# Revit family: ATPSF-101-120-S REV2
name_source: partatom
category: Mechanical Equipment
revit_build: Autodesk Revit 2017 (Build: 20190508_0315(x64)
units: mm (PartAtom-declared; Revit-internal decimal feet)

## family parameters
Always vertical = Yes
Cut with Voids When Loaded = No
OmniClass Number = 23.75.00.00
OmniClass Title = Climate Control (HVAC)
Part Type = Normal
Room Calculation Point = No
Round Connector Dimension = Use Diameter
Shared = No
Work Plane-Based = No

## types (10) — shared parameters
1-1/2HP = No
2HP = No
Base Height = 5' - 9 7/8"
Base Lenglth = 2' - 6 1/2"
Base Width = 1' - 10 1/2"
Description = Automatic Fuel Oil Transfer Pump Set
Inlet Diameter = 0' - 1"
Inlet Radius = 0' - 0 1/2"
Manufacturer = Preferred Utilities MFG
Outlet Diameter = 0' - 0 1/2"
Outlet Radius = 0' - 0 1/4"
Relief Valve Diameter = 0' - 0 1/2"
Relief Valve Radius = 0' - 0 1/4"
URL = www.preferred-mfg.com
Weight = 450.00 lbf

## per-type parameters (varying)
| type | 1/2HP | 1/3HP | 115/208/230 Volts | 1HP | 208/230/460 Volts | 3/4HP | G.P.H. Oil #2 / #4 | HP | Model | PSI | Phase | RPM |
| 101-S_23/24 GPH_100 PSI_1/3 HP_1725 RPM | No | Yes | Yes | No | No | No | 23 / 24 | 1/3 | ATPSF-101-S | 100.00 psi | 1 | 1725 |
| 101-S_24/25 GPH_50 PSI_1/3 HP_1725 RPM | No | Yes | Yes | No | No | No | 24 / 25 | 1/3 | ATPSF-101-S | 50.00 psi | 1 | 1725 |
| 102-S_51/54 GPH_100 PSI_1/3 HP_1725 RPM | No | Yes | Yes | No | No | No | 51 / 54 | 1/3 | ATPSF-102-S | 100.00 psi | 1 | 1725 |
| 102-S_54/56 GPH_50 PSI_1/3 HP_1725 RPM | No | Yes | Yes | No | No | No | 54 / 56 | 1/3 | ATPSF-102-S | 50.00 psi | 1 | 1725 |
| 103-S_89/96 GPH_100 PSI_1/3 HP_1725 RPM | No | Yes | Yes | No | No | No | 89 / 96 | 1/3 | ATPSF-103-S | 100.00 psi | 1 | 1725 |
| 103-S_97/100 GPH_50 PSI_1/3 HP_1725 RPM | No | Yes | Yes | No | No | No | 97 / 100 | 1/3 | ATPSF-103-S | 50.00 psi | 1 | 1725 |
| 104-S_150/161 GPH_100 PSI_1/2 HP_1725 RPM | Yes | No | No | No | Yes | No | 150 / 161 | 1/2 | ATPSF-104-S | 100.00 psi | 3 | 1725 |
| 104-S_163/169 GPH_50 PSI_1/2 HP_1725 RPM | Yes | No | No | No | Yes | No | 163 / 169 | 1/2 | ATPSF-104-S | 50.00 psi | 3 | 1725 |
| 105-S_328/344 GPH_50 PSI_3/4 HP_1725 RPM | No | No | No | No | Yes | Yes | 328 / 344 | 3/4 | ATPSF-105-S | 50.00 psi | 3 | 1725 |
| 106-S_305/337 GPH_100 PSI_1 HP_1760 RPM | No | No | No | Yes | Yes | No | 305 / 337 | 1 | ATPSF-106-S | 100.00 psi | 3 | 1760 |

## geometry (parser evidence)
native form markers: Sweep x2
no freeform markers — native parametric forms only
